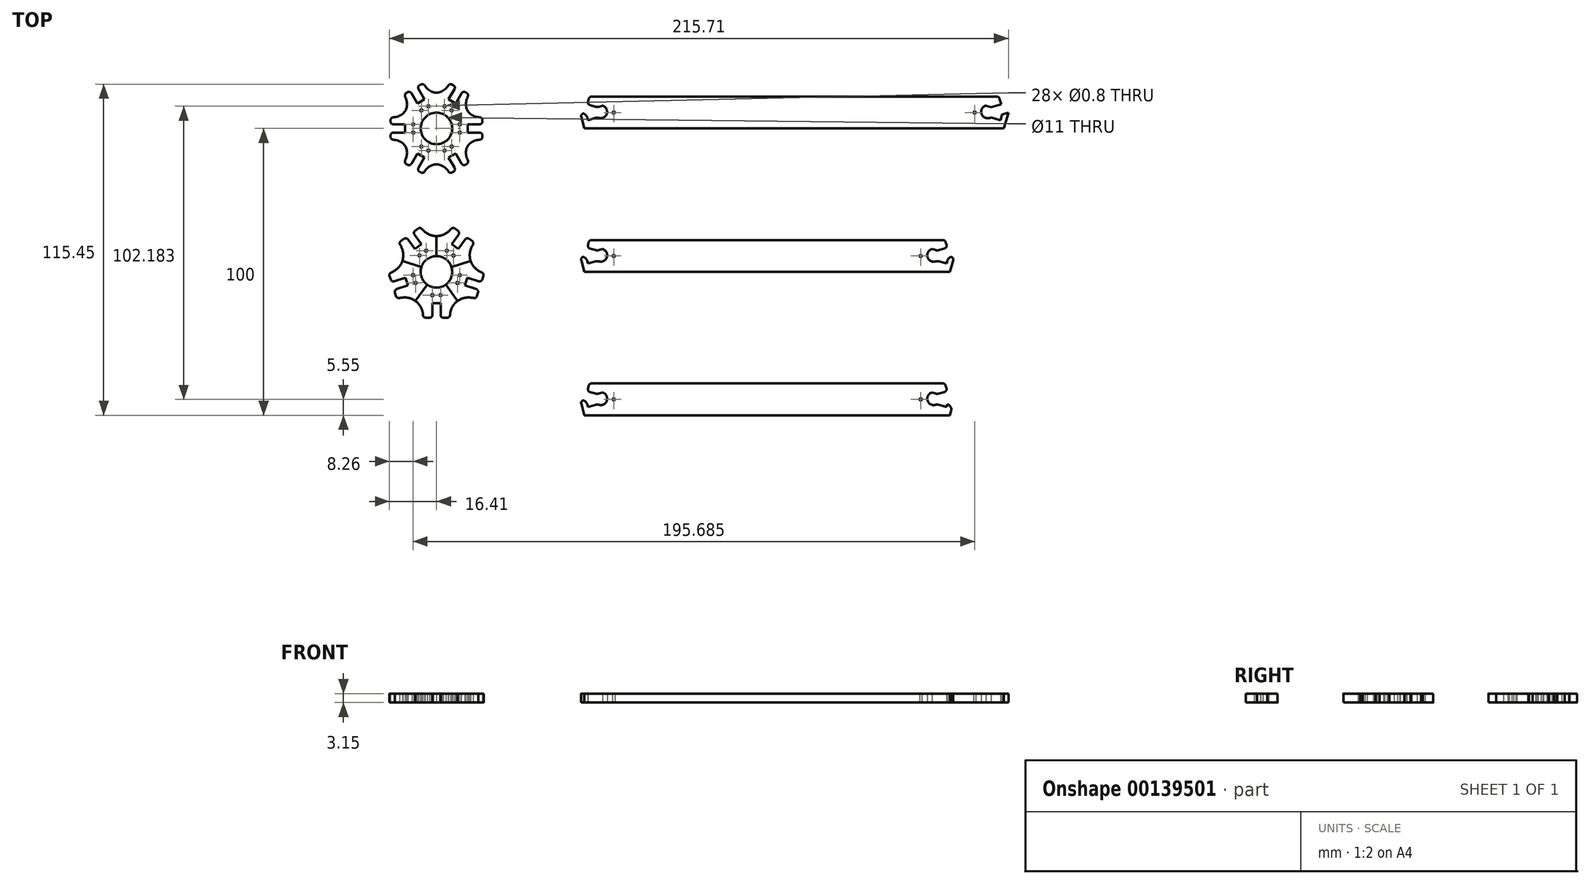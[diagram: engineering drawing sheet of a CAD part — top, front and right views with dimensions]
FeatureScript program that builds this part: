
annotation { "Feature Type Name" : "Feature", "Feature Type Description" : "" }
export const myFeature = defineFeature(function(context is Context, id is Id, definition is map)
    precondition{}
    {
        {
            assignVariable(context, id + "F0", {"name" : "wood_thickness", "anyValue" : 3.15 * mm});
        }
        {
            var Q0;
            Q0=qCreatedBy(makeId("Top.planeOp"),FACE);
            var sketch = newSketch(context, id + "F1", { "sketchPlane" : qUnion([Q0])});
            skArc(sketch, "E0", {"start": v(4.76, 2.75) * mm, "mid": v(2.75, 4.76) * mm, "end": v(0, 5.5) * mm});
            skArc(sketch, "E1", {"start": v(9.44, 5.45) * mm, "mid": v(5.45, 9.44) * mm, "end": v(0, 10.9) * mm, "construction": true});
            skLineSegment(sketch, "E2", {"start": v(0, 0) * mm, "end": v(0, 20) * mm, "construction": true});
            skLineSegment(sketch, "E3", {"start": v(0, 0) * mm, "end": v(17.32, 10) * mm, "construction": true});
            skPoint(sketch, "E4", {"position": v(0, 10.9) * mm});
            skPoint(sketch, "E5", {"position": v(0, 5.5) * mm});
            skPoint(sketch, "E6", {"position": v(9.44, 5.45) * mm});
            skPoint(sketch, "E7", {"position": v(4.76, 2.75) * mm});
            skLineSegment(sketch, "E8", {"start": v(5.48, 15.31) * mm, "end": v(5.9, 15.07) * mm});
            skLineSegment(sketch, "E9", {"start": v(6.27, 13.7) * mm, "end": v(4.22, 10.15) * mm});
            skLineSegment(sketch, "E10", {"start": v(6.68, 8.73) * mm, "end": v(8.73, 12.28) * mm});
            skLineSegment(sketch, "E11", {"start": v(10.1, 12.64) * mm, "end": v(10.52, 12.4) * mm});
            skPoint(sketch, "E12", {"position": v(0, 12.5) * mm});
            skEllipticalArc(sketch, "E13", {});
            skLineSegment(sketch, "E14", {"start": v(4.76, 2.75) * mm, "end": v(9.44, 5.45) * mm});
            skLineSegment(sketch, "E15", {"start": v(0, 5.5) * mm, "end": v(0, 10.9) * mm});
            skArc(sketch, "E16", {"start": v(10.83, 6.25) * mm, "mid": v(6.25, 10.83) * mm, "end": v(0, 12.5) * mm, "construction": true});
            skEllipticalArc(sketch, "E17", {});
            skLineSegment(sketch, "E18", {"start": v(0, 10.9) * mm, "end": v(0, 12.5) * mm});
            skLineSegment(sketch, "E19", {"start": v(9.44, 5.45) * mm, "end": v(10.83, 6.25) * mm});
            skPoint(sketch, "E20.visualSharp", {"position": v(4.62, 15.81) * mm});
            skArc(sketch, "E20.filletArc", {"start": v(5.48, 15.31) * mm, "mid": v(4.75, 15.42) * mm, "end": v(4.15, 15) * mm});
            skPoint(sketch, "E21.visualSharp", {"position": v(6.77, 14.57) * mm});
            skArc(sketch, "E21.filletArc", {"start": v(6.27, 13.7) * mm, "mid": v(6.37, 14.46) * mm, "end": v(5.9, 15.07) * mm});
            skLineSegment(sketch, "E22", {"start": v(4.15, 15) * mm, "end": v(6.3, 13.76) * mm, "construction": true});
            skLineSegment(sketch, "E23", {"start": v(4.15, 15) * mm, "end": v(4.62, 15.81) * mm, "construction": true});
            skLineSegment(sketch, "E24", {"start": v(4.62, 15.81) * mm, "end": v(5.48, 15.31) * mm, "construction": true});
            skArc(sketch, "E25.filletArc", {"start": v(10.92, 11.1) * mm, "mid": v(10.98, 11.82) * mm, "end": v(10.52, 12.4) * mm});
            skLineSegment(sketch, "E26", {"start": v(10.52, 12.4) * mm, "end": v(11.38, 11.9) * mm, "construction": true});
            skLineSegment(sketch, "E27", {"start": v(11.38, 11.9) * mm, "end": v(10.92, 11.1) * mm, "construction": true});
            skPoint(sketch, "E28.visualSharp", {"position": v(9.23, 13.14) * mm});
            skArc(sketch, "E28.filletArc", {"start": v(10.1, 12.64) * mm, "mid": v(9.34, 12.74) * mm, "end": v(8.73, 12.28) * mm});
            skLineSegment(sketch, "E29", {"start": v(4.22, 10.15) * mm, "end": v(5.45, 9.44) * mm});
            skLineSegment(sketch, "E30", {"start": v(5.45, 9.44) * mm, "end": v(6.68, 8.73) * mm});
            skLineSegment(sketch, "E31", {"start": v(10.92, 11.1) * mm, "end": v(8.77, 12.33) * mm, "construction": true});
            skLineSegment(sketch, "E32", {"start": v(4.22, 10.15) * mm, "end": v(1.42, 5.31) * mm, "construction": true});
            skLineSegment(sketch, "E33", {"start": v(3.9, 3.89) * mm, "end": v(6.68, 8.73) * mm, "construction": true});
            skCircle(sketch, "E34", {"center": v(2.82, 7.73) * mm, "radius": 0.4 * mm});
            skCircle(sketch, "E35", {"center": v(5.29, 6.3) * mm, "radius": 0.4 * mm});
            const initialGuessF1  = {"E13": [0, 0.02, 0, -1, 0.0075, 0.005564135286728559, 0, 0.8408323808141549], "E17": [0.017320508075688766, 0.01, -0.8660254037844385, -0.5, 0.0075, 0.005564135286728561, 5.44235292636543, 0]};
            skSetInitialGuess(sketch, initialGuessF1);
            skSolve(sketch);
        }
        {
            var Q0;
            Q0=makeQuery(id+"F1.imprint","IMPRINT",FACE,{"disambiguationData":[TD([[makeQuery(id+"F1.imprint","IMPRINT",EDGE,{"derivedFrom":sQuery(id+"F1.wireOp",EDGE,"E0")}),-1.0]])]});
            extrude(context, id + "F2", {"entities" : qUnion([Q0]), "depth" : getVariable(context, 'wood_thickness')});
        }
        {
            var Q0;
            Q0=qCreatedBy(makeId("Front.planeOp"),FACE);
            var sketch = newSketch(context, id + "F3", { "sketchPlane" : qUnion([Q0])});
            skLineSegment(sketch, "E36", {"start": v(0, 0) * mm, "end": v(0, 20) * mm});
            skSolve(sketch);
        }
        {
            var Q0;
            Q0=makeQuery(id+"F2.opExtrude","SWEPT_BODY",BODY,{"disambiguationData":[OSD([sQuery(id+"F1.wireOp",EDGE,"E0"),sQuery(id+"F1.wireOp",EDGE,"E8"),sQuery(id+"F1.wireOp",EDGE,"E9"),sQuery(id+"F1.wireOp",EDGE,"mfKBiNOg-JzFv-5jMB-imMp-SPBcFm9SmBFP"),sQuery(id+"F1.wireOp",EDGE,"E10"),sQuery(id+"F1.wireOp",EDGE,"E11"),sQuery(id+"F1.wireOp",EDGE,"E13"),sQuery(id+"F1.wireOp",EDGE,"E14"),sQuery(id+"F1.wireOp",EDGE,"E15"),sQuery(id+"F1.wireOp",EDGE,"E17"),sQuery(id+"F1.wireOp",EDGE,"E18"),sQuery(id+"F1.wireOp",EDGE,"E19")])]});
            var Q1;
            Q1=sQuery(id+"F3.wireOp",EDGE,"E36");
            circularPattern(context, id + "F4", {"operationType" : NewBodyOperationType.ADD, "entities" : qUnion([Q0]), "axis" : qUnion([Q1]), "angle" : 60 * degree, "instanceCount" : 6, "oppositeDirection" : true});
        }
        {
            var Q0;
            Q0=qCreatedBy(makeId("Top.planeOp"),FACE);
            var sketch = newSketch(context, id + "F5", { "sketchPlane" : qUnion([Q0])});
            skArc(sketch, "E37", {"start": v(5.23, -48.3) * mm, "mid": v(3.23, -45.55) * mm, "end": v(0, -44.5) * mm});
            skArc(sketch, "E38", {"start": v(10.37, -46.63) * mm, "mid": v(6.4, -41.18) * mm, "end": v(0, -39.1) * mm, "construction": true});
            skLineSegment(sketch, "E39", {"start": v(0, -50) * mm, "end": v(0, -30) * mm, "construction": true});
            skLineSegment(sketch, "E40", {"start": v(0, -50) * mm, "end": v(19.02, -43.82) * mm, "construction": true});
            skPoint(sketch, "E41", {"position": v(0, -39.1) * mm});
            skPoint(sketch, "E42", {"position": v(0, -44.5) * mm});
            skPoint(sketch, "E43", {"position": v(10.37, -46.63) * mm});
            skPoint(sketch, "E44", {"position": v(5.23, -48.3) * mm});
            skLineSegment(sketch, "E45", {"start": v(6.4, -34.88) * mm, "end": v(7.44, -35.63) * mm});
            skLineSegment(sketch, "E46", {"start": v(7.66, -37.03) * mm, "end": v(5.25, -40.34) * mm});
            skLineSegment(sketch, "E47", {"start": v(7.56, -42.02) * mm, "end": v(9.97, -38.7) * mm});
            skLineSegment(sketch, "E48", {"start": v(11.37, -38.48) * mm, "end": v(12.4, -39.23) * mm});
            skPoint(sketch, "E49", {"position": v(0, -37.5) * mm});
            skEllipticalArc(sketch, "E50", {});
            skLineSegment(sketch, "E51", {"start": v(5.23, -48.3) * mm, "end": v(10.37, -46.63) * mm});
            skLineSegment(sketch, "E52", {"start": v(0, -44.5) * mm, "end": v(0, -39.1) * mm});
            skArc(sketch, "E53", {"start": v(11.89, -46.14) * mm, "mid": v(7.35, -39.89) * mm, "end": v(0, -37.5) * mm, "construction": true});
            skEllipticalArc(sketch, "E54", {});
            skLineSegment(sketch, "E55", {"start": v(0, -39.1) * mm, "end": v(0, -37.5) * mm});
            skLineSegment(sketch, "E56", {"start": v(10.37, -46.63) * mm, "end": v(11.89, -46.14) * mm});
            skPoint(sketch, "E57.visualSharp", {"position": v(5.6, -34.3) * mm});
            skArc(sketch, "E57.filletArc", {"start": v(6.4, -34.88) * mm, "mid": v(5.7, -34.7) * mm, "end": v(5.05, -35.05) * mm});
            skPoint(sketch, "E58.visualSharp", {"position": v(8.25, -36.22) * mm});
            skArc(sketch, "E58.filletArc", {"start": v(7.66, -37.03) * mm, "mid": v(7.84, -36.28) * mm, "end": v(7.44, -35.63) * mm});
            skLineSegment(sketch, "E59", {"start": v(5.05, -35.05) * mm, "end": v(7.7, -36.98) * mm, "construction": true});
            skLineSegment(sketch, "E60", {"start": v(5.05, -35.05) * mm, "end": v(5.6, -34.3) * mm, "construction": true});
            skLineSegment(sketch, "E61", {"start": v(5.6, -34.3) * mm, "end": v(6.4, -34.88) * mm, "construction": true});
            skArc(sketch, "E62.filletArc", {"start": v(12.66, -40.58) * mm, "mid": v(12.8, -39.86) * mm, "end": v(12.4, -39.23) * mm});
            skLineSegment(sketch, "E63", {"start": v(12.4, -39.23) * mm, "end": v(13.21, -39.82) * mm, "construction": true});
            skLineSegment(sketch, "E64", {"start": v(13.21, -39.82) * mm, "end": v(12.66, -40.58) * mm, "construction": true});
            skPoint(sketch, "E65.visualSharp", {"position": v(10.56, -37.9) * mm});
            skArc(sketch, "E65.filletArc", {"start": v(11.37, -38.48) * mm, "mid": v(10.62, -38.3) * mm, "end": v(9.97, -38.7) * mm});
            skLineSegment(sketch, "E66", {"start": v(5.25, -40.34) * mm, "end": v(6.4, -41.18) * mm});
            skLineSegment(sketch, "E67", {"start": v(6.4, -41.18) * mm, "end": v(7.56, -42.02) * mm});
            skLineSegment(sketch, "E68", {"start": v(12.66, -40.58) * mm, "end": v(10, -38.65) * mm, "construction": true});
            skLineSegment(sketch, "E69", {"start": v(5.25, -40.34) * mm, "end": v(1.97, -44.86) * mm, "construction": true});
            skLineSegment(sketch, "E70", {"start": v(4.28, -46.54) * mm, "end": v(7.56, -42.02) * mm, "construction": true});
            skCircle(sketch, "E71", {"center": v(3.61, -42.6) * mm, "radius": 0.4 * mm});
            skCircle(sketch, "E72", {"center": v(5.92, -44.28) * mm, "radius": 0.4 * mm});
            const initialGuessF5  = {"E50": [0, -0.03, 0, -1, 0.0075, 0.006825802079921419, 0, 0.832408500908553], "E54": [0.019021130325903073, -0.043819660112501053, -0.9510565162951536, -0.3090169943749476, 0.0075, 0.006825802079921406, 5.450776806271033, 0]};
            skSetInitialGuess(sketch, initialGuessF5);
            skSolve(sketch);
        }
        {
            var Q0;
            Q0=makeQuery(id+"F5.imprint","IMPRINT",FACE,{"disambiguationData":[TD([[makeQuery(id+"F5.imprint","IMPRINT",EDGE,{"derivedFrom":sQuery(id+"F5.wireOp",EDGE,"E37")}),-1.0]])]});
            extrude(context, id + "F6", {"entities" : qUnion([Q0]), "depth" : getVariable(context, 'wood_thickness')});
        }
        {
            var Q0;
            Q0=qCreatedBy(makeId("Front.planeOp"),FACE);
            var Q1;
            Q1=sQuery(id+"F5.wireOp",VERTEX,"E40.start");
            cPlane(context, id + "F7", {"entities" : qUnion([Q0, Q1]), "cplaneType" : CPlaneType.PLANE_POINT, "offset" : 25 * mm, "width" : 150 * mm, "height" : 150 * mm});
        }
        {
            var Q0;
            Q0=qCreatedBy(id+"F7.planeOp",FACE);
            var sketch = newSketch(context, id + "F8", { "sketchPlane" : qUnion([Q0])});
            skLineSegment(sketch, "E73", {"start": v(0, 0) * mm, "end": v(0, 50) * mm});
            skSolve(sketch);
        }
        {
            var Q0;
            Q0=makeQuery(id+"F6.opExtrude","SWEPT_BODY",BODY,{"disambiguationData":[OSD([sQuery(id+"F5.wireOp",EDGE,"E37"),sQuery(id+"F5.wireOp",EDGE,"E45"),sQuery(id+"F5.wireOp",EDGE,"E46"),sQuery(id+"F5.wireOp",EDGE,"E47"),sQuery(id+"F5.wireOp",EDGE,"E48"),sQuery(id+"F5.wireOp",EDGE,"E50"),sQuery(id+"F5.wireOp",EDGE,"E51"),sQuery(id+"F5.wireOp",EDGE,"E52"),sQuery(id+"F5.wireOp",EDGE,"E54"),sQuery(id+"F5.wireOp",EDGE,"E55"),sQuery(id+"F5.wireOp",EDGE,"E56"),sQuery(id+"F5.wireOp",EDGE,"E57.filletArc"),sQuery(id+"F5.wireOp",EDGE,"E58.filletArc"),sQuery(id+"F5.wireOp",EDGE,"E62.filletArc"),sQuery(id+"F5.wireOp",EDGE,"E65.filletArc"),sQuery(id+"F5.wireOp",EDGE,"E66"),sQuery(id+"F5.wireOp",EDGE,"E67"),sQuery(id+"F5.wireOp",EDGE,"E71"),sQuery(id+"F5.wireOp",EDGE,"E72")])]});
            var Q1;
            Q1=sQuery(id+"F8.wireOp",EDGE,"E73");
            circularPattern(context, id + "F9", {"operationType" : NewBodyOperationType.ADD, "entities" : qUnion([Q0]), "axis" : qUnion([Q1]), "angle" : 72 * degree, "instanceCount" : 5});
        }
        {
            var Q0;
            Q0=qCreatedBy(makeId("Top.planeOp"),FACE);
            var sketch = newSketch(context, id + "F10", { "sketchPlane" : qUnion([Q0])});
            skLineSegment(sketch, "E74", {"start": v(0, 0) * mm, "end": v(50, 0) * mm, "construction": true});
            skLineSegment(sketch, "E75", {"start": v(50, 0) * mm, "end": v(50, 11.1) * mm, "construction": true});
            skLineSegment(sketch, "E76", {"start": v(50, 0) * mm, "end": v(124.65, 0) * mm, "construction": true});
            skLineSegment(sketch, "E77", {"start": v(50, 11.1) * mm, "end": v(124.65, 11.1) * mm, "construction": true});
            skLineSegment(sketch, "E78", {"start": v(124.65, 11.1) * mm, "end": v(124.65, 0) * mm, "construction": true});
            skLineSegment(sketch, "E79", {"start": v(51.6, 0) * mm, "end": v(50, 5.55) * mm});
            skLineSegment(sketch, "E80", {"start": v(50, 5.55) * mm, "end": v(52.19, 4.92) * mm});
            skLineSegment(sketch, "E81", {"start": v(52.19, 4.92) * mm, "end": v(52.77, 2.9) * mm});
            skLineSegment(sketch, "E82", {"start": v(52.77, 2.9) * mm, "end": v(56, 3.83) * mm});
            skLineSegment(sketch, "E83", {"start": v(56, 3.83) * mm, "end": v(56.6, 3.66) * mm});
            skLineSegment(sketch, "E84", {"start": v(56.6, 3.66) * mm, "end": v(58.92, 4.32) * mm, "construction": true});
            skLineSegment(sketch, "E85", {"start": v(58.92, 4.32) * mm, "end": v(57.87, 7.95) * mm, "construction": true});
            skLineSegment(sketch, "E86", {"start": v(57.87, 7.95) * mm, "end": v(56, 7.42) * mm});
            skLineSegment(sketch, "E87", {"start": v(56, 7.42) * mm, "end": v(52.5, 8.42) * mm});
            skLineSegment(sketch, "E88", {"start": v(52.5, 8.42) * mm, "end": v(53.27, 11.1) * mm});
            skLineSegment(sketch, "E89", {"start": v(51.6, 0) * mm, "end": v(197.7, 0) * mm});
            skLineSegment(sketch, "E90", {"start": v(53.27, 11.1) * mm, "end": v(196.03, 11.1) * mm});
            skLineSegment(sketch, "E91", {"start": v(56.6, 3.66) * mm, "end": v(57.87, 7.95) * mm, "construction": true});
            skArc(sketch, "E92", {"start": v(57.87, 7.95) * mm, "mid": v(59.39, 5.17) * mm, "end": v(56.6, 3.66) * mm});
            skPoint(sketch, "E93.endSnap0", {"position": v(51.1, 5.24) * mm});
            skLineSegment(sketch, "E94.MirrorCS", {"start": v(197.7, 0) * mm, "end": v(199.3, 5.55) * mm});
            skLineSegment(sketch, "E95.MirrorCS", {"start": v(199.3, 5.55) * mm, "end": v(197.11, 4.92) * mm});
            skLineSegment(sketch, "E96.MirrorCS", {"start": v(197.11, 4.92) * mm, "end": v(196.53, 2.9) * mm});
            skLineSegment(sketch, "E97.MirrorCS", {"start": v(196.53, 2.9) * mm, "end": v(193.3, 3.83) * mm});
            skLineSegment(sketch, "E98.MirrorCS", {"start": v(193.3, 3.83) * mm, "end": v(192.7, 3.66) * mm});
            skArc(sketch, "E99.MirrorCS", {"start": v(191.43, 7.95) * mm, "mid": v(189.91, 5.17) * mm, "end": v(192.7, 3.66) * mm});
            skLineSegment(sketch, "E100.MirrorCS", {"start": v(191.43, 7.95) * mm, "end": v(193.3, 7.42) * mm});
            skLineSegment(sketch, "E101.MirrorCS", {"start": v(193.3, 7.42) * mm, "end": v(196.8, 8.42) * mm});
            skLineSegment(sketch, "E102.MirrorCS", {"start": v(196.8, 8.42) * mm, "end": v(196.03, 11.1) * mm});
            skLineSegment(sketch, "E103", {"start": v(50, 5.55) * mm, "end": v(199.3, 5.55) * mm, "construction": true});
            skCircle(sketch, "E104", {"center": v(187.54, 5.55) * mm, "radius": 0.4 * mm});
            skCircle(sketch, "E105", {"center": v(61.76, 5.55) * mm, "radius": 0.4 * mm});
            skLineSegment(sketch, "E106", {"start": v(61.76, 5.55) * mm, "end": v(59.46, 5.55) * mm, "construction": true});
            skLineSegment(sketch, "E107", {"start": v(187.54, 5.55) * mm, "end": v(189.84, 5.55) * mm, "construction": true});
            skSolve(sketch);
        }
        {
            var Q0;
            Q0=makeQuery(id+"F10.imprint","IMPRINT",FACE,{"disambiguationData":[TD([[makeQuery(id+"F10.imprint","IMPRINT",EDGE,{"derivedFrom":sQuery(id+"F10.wireOp",EDGE,"E79")}),-1.0]])]});
            extrude(context, id + "F11", {"entities" : qUnion([Q0]), "depth" : getVariable(context, 'wood_thickness')});
        }
        {
            var Q0;
            Q0=makeQuery(id+"F11.opExtrude","SWEPT_EDGE",EDGE,{"disambiguationData":[OSD([sQuery(id+"F10.wireOp",EDGE,"E86"),sQuery(id+"F10.wireOp",EDGE,"E87")])]});
            var Q1;
            Q1=makeQuery(id+"F11.opExtrude","SWEPT_EDGE",EDGE,{"disambiguationData":[OSD([sQuery(id+"F10.wireOp",EDGE,"E82"),sQuery(id+"F10.wireOp",EDGE,"E83")])]});
            var Q2;
            Q2=makeQuery(id+"F11.opExtrude","SWEPT_EDGE",EDGE,{"disambiguationData":[OSD([sQuery(id+"F10.wireOp",EDGE,"E80"),sQuery(id+"F10.wireOp",EDGE,"E81")])]});
            var Q3;
            Q3=makeQuery(id+"F11.opExtrude","SWEPT_EDGE",EDGE,{"disambiguationData":[OSD([sQuery(id+"F10.wireOp",EDGE,"ecbd6355-1247-42db-afb2-b917e20613ce0.MirrorCS"),sQuery(id+"F10.wireOp",EDGE,"ef6c834d-02ef-4d6f-9716-54fc313d26910.MirrorCS")])]});
            var Q4;
            Q4=makeQuery(id+"F11.opExtrude","SWEPT_EDGE",EDGE,{"disambiguationData":[OSD([sQuery(id+"F10.wireOp",EDGE,"c2f2e863-0dd1-41ea-9a90-eeab5b9333880.MirrorCS"),sQuery(id+"F10.wireOp",EDGE,"853300a5-473e-431b-ac92-eafcaa067bd40.MirrorCS")])]});
            var Q5;
            Q5=makeQuery(id+"F11.opExtrude","SWEPT_EDGE",EDGE,{"disambiguationData":[OSD([sQuery(id+"F10.wireOp",EDGE,"4ca5c7fb-cf56-4dfb-8872-57cf61e489230.MirrorCS"),sQuery(id+"F10.wireOp",EDGE,"298d15c9-40d8-42b4-a12f-17c602055c9c0.MirrorCS")])]});
            fillet(context, id + "F12", {"entities" : qUnion([Q0, Q1, Q2, Q3, Q4, Q5]), "radius" : 2 * mm, "tangentPropagation" : true, "allowEdgeOverflow" : false});
        }
        {
            var Q0;
            Q0=makeQuery(id+"F11.opExtrude","SWEPT_EDGE",EDGE,{"disambiguationData":[OSD([sQuery(id+"F10.wireOp",EDGE,"E79"),sQuery(id+"F10.wireOp",EDGE,"E80")])]});
            var Q1;
            Q1=makeQuery(id+"F11.opExtrude","SWEPT_EDGE",EDGE,{"disambiguationData":[OSD([sQuery(id+"F10.wireOp",EDGE,"E87"),sQuery(id+"F10.wireOp",EDGE,"E88")])]});
            var Q2;
            Q2=makeQuery(id+"F11.opExtrude","SWEPT_EDGE",EDGE,{"disambiguationData":[OSD([sQuery(id+"F10.wireOp",EDGE,"E88"),sQuery(id+"F10.wireOp",EDGE,"E90")])]});
            var Q3;
            Q3=makeQuery(id+"F11.opExtrude","SWEPT_EDGE",EDGE,{"disambiguationData":[OSD([sQuery(id+"F10.wireOp",EDGE,"58fe3ff1-e28c-4c06-9c65-c541867c6f450.MirrorCS"),sQuery(id+"F10.wireOp",EDGE,"4ca5c7fb-cf56-4dfb-8872-57cf61e489230.MirrorCS")])]});
            var Q4;
            Q4=makeQuery(id+"F11.opExtrude","SWEPT_EDGE",EDGE,{"disambiguationData":[OSD([sQuery(id+"F10.wireOp",EDGE,"853300a5-473e-431b-ac92-eafcaa067bd40.MirrorCS"),sQuery(id+"F10.wireOp",EDGE,"cfe77f50-aeba-4152-badc-bec2262164020.MirrorCS")])]});
            var Q5;
            Q5=makeQuery(id+"F11.opExtrude","SWEPT_EDGE",EDGE,{"disambiguationData":[OSD([sQuery(id+"F10.wireOp",EDGE,"cfe77f50-aeba-4152-badc-bec2262164020.MirrorCS"),sQuery(id+"F10.wireOp",EDGE,"E90")])]});
            fillet(context, id + "F13", {"entities" : qUnion([Q0, Q1, Q2, Q3, Q4, Q5]), "radius" : 1 * mm, "tangentPropagation" : true, "allowEdgeOverflow" : false});
        }
        {
            var Q0;
            Q0=qCreatedBy(makeId("Top.planeOp"),FACE);
            var sketch = newSketch(context, id + "F14", { "sketchPlane" : qUnion([Q0])});
            skLineSegment(sketch, "E108", {"start": v(0, -50) * mm, "end": v(50, -50) * mm, "construction": true});
            skLineSegment(sketch, "E109", {"start": v(50, -50) * mm, "end": v(50, -38.9) * mm, "construction": true});
            skLineSegment(sketch, "E110", {"start": v(50, -50) * mm, "end": v(115.25, -50) * mm, "construction": true});
            skLineSegment(sketch, "E111", {"start": v(50, -38.9) * mm, "end": v(115.25, -38.9) * mm, "construction": true});
            skLineSegment(sketch, "E112", {"start": v(115.25, -38.9) * mm, "end": v(115.25, -50) * mm, "construction": true});
            skLineSegment(sketch, "E113", {"start": v(51.6, -50) * mm, "end": v(50, -44.45) * mm});
            skLineSegment(sketch, "E114", {"start": v(50, -44.45) * mm, "end": v(52.19, -45.08) * mm});
            skLineSegment(sketch, "E115", {"start": v(52.19, -45.08) * mm, "end": v(52.77, -47.1) * mm});
            skLineSegment(sketch, "E116", {"start": v(52.77, -47.1) * mm, "end": v(56, -46.17) * mm});
            skLineSegment(sketch, "E117", {"start": v(56, -46.17) * mm, "end": v(56.6, -46.34) * mm});
            skLineSegment(sketch, "E118", {"start": v(56.6, -46.34) * mm, "end": v(58.92, -45.68) * mm, "construction": true});
            skLineSegment(sketch, "E119", {"start": v(58.92, -45.68) * mm, "end": v(57.87, -42.05) * mm, "construction": true});
            skLineSegment(sketch, "E120", {"start": v(57.87, -42.05) * mm, "end": v(56, -42.58) * mm});
            skLineSegment(sketch, "E121", {"start": v(56, -42.58) * mm, "end": v(52.5, -41.58) * mm});
            skLineSegment(sketch, "E122", {"start": v(52.5, -41.58) * mm, "end": v(53.27, -38.9) * mm});
            skLineSegment(sketch, "E123", {"start": v(51.6, -50) * mm, "end": v(178.9, -50) * mm});
            skLineSegment(sketch, "E124", {"start": v(53.27, -38.9) * mm, "end": v(177.23, -38.9) * mm});
            skLineSegment(sketch, "E125", {"start": v(56.6, -46.34) * mm, "end": v(57.87, -42.05) * mm, "construction": true});
            skArc(sketch, "E126", {"start": v(57.87, -42.05) * mm, "mid": v(59.39, -44.83) * mm, "end": v(56.6, -46.34) * mm});
            skPoint(sketch, "E127.endSnap0", {"position": v(51.1, -44.76) * mm});
            skLineSegment(sketch, "E128.MirrorCS", {"start": v(178.9, -50) * mm, "end": v(180.5, -44.45) * mm});
            skLineSegment(sketch, "E129.MirrorCS", {"start": v(180.5, -44.45) * mm, "end": v(178.31, -45.08) * mm});
            skLineSegment(sketch, "E130.MirrorCS", {"start": v(178.31, -45.08) * mm, "end": v(177.73, -47.1) * mm});
            skLineSegment(sketch, "E131.MirrorCS", {"start": v(177.73, -47.1) * mm, "end": v(174.5, -46.17) * mm});
            skLineSegment(sketch, "E132.MirrorCS", {"start": v(174.5, -46.17) * mm, "end": v(173.9, -46.34) * mm});
            skArc(sketch, "E133.MirrorCS", {"start": v(172.63, -42.05) * mm, "mid": v(171.11, -44.83) * mm, "end": v(173.9, -46.34) * mm});
            skLineSegment(sketch, "E134.MirrorCS", {"start": v(172.63, -42.05) * mm, "end": v(174.5, -42.58) * mm});
            skLineSegment(sketch, "E135.MirrorCS", {"start": v(174.5, -42.58) * mm, "end": v(178, -41.58) * mm});
            skLineSegment(sketch, "E136.MirrorCS", {"start": v(178, -41.58) * mm, "end": v(177.23, -38.9) * mm});
            skLineSegment(sketch, "E137", {"start": v(50, -44.45) * mm, "end": v(180.5, -44.45) * mm, "construction": true});
            skCircle(sketch, "E138", {"center": v(168.74, -44.45) * mm, "radius": 0.4 * mm});
            skCircle(sketch, "E139", {"center": v(61.76, -44.45) * mm, "radius": 0.4 * mm});
            skLineSegment(sketch, "E140", {"start": v(61.76, -44.45) * mm, "end": v(59.46, -44.45) * mm, "construction": true});
            skLineSegment(sketch, "E141", {"start": v(168.74, -44.45) * mm, "end": v(171.04, -44.45) * mm, "construction": true});
            skLineSegment(sketch, "E142", {"start": v(0, -50) * mm, "end": v(0, 0) * mm, "construction": true});
            skSolve(sketch);
        }
        {
            var Q0;
            Q0=makeQuery(id+"F14.imprint","IMPRINT",FACE,{"disambiguationData":[TD([[makeQuery(id+"F14.imprint","IMPRINT",EDGE,{"derivedFrom":sQuery(id+"F14.wireOp",EDGE,"E113")}),-1.0]])]});
            extrude(context, id + "F15", {"entities" : qUnion([Q0]), "depth" : getVariable(context, 'wood_thickness')});
        }
        {
            var Q0;
            Q0=makeQuery(id+"F15.opExtrude","SWEPT_EDGE",EDGE,{"disambiguationData":[OSD([sQuery(id+"F14.wireOp",EDGE,"E114"),sQuery(id+"F14.wireOp",EDGE,"E115")])]});
            var Q1;
            Q1=makeQuery(id+"F15.opExtrude","SWEPT_EDGE",EDGE,{"disambiguationData":[OSD([sQuery(id+"F14.wireOp",EDGE,"E116"),sQuery(id+"F14.wireOp",EDGE,"E117")])]});
            var Q2;
            Q2=makeQuery(id+"F15.opExtrude","SWEPT_EDGE",EDGE,{"disambiguationData":[OSD([sQuery(id+"F14.wireOp",EDGE,"E120"),sQuery(id+"F14.wireOp",EDGE,"E121")])]});
            var Q3;
            Q3=makeQuery(id+"F15.opExtrude","SWEPT_EDGE",EDGE,{"disambiguationData":[OSD([sQuery(id+"F14.wireOp",EDGE,"E134.MirrorCS"),sQuery(id+"F14.wireOp",EDGE,"E135.MirrorCS")])]});
            var Q4;
            Q4=makeQuery(id+"F15.opExtrude","SWEPT_EDGE",EDGE,{"disambiguationData":[OSD([sQuery(id+"F14.wireOp",EDGE,"E131.MirrorCS"),sQuery(id+"F14.wireOp",EDGE,"E132.MirrorCS")])]});
            var Q5;
            Q5=makeQuery(id+"F15.opExtrude","SWEPT_EDGE",EDGE,{"disambiguationData":[OSD([sQuery(id+"F14.wireOp",EDGE,"E129.MirrorCS"),sQuery(id+"F14.wireOp",EDGE,"E130.MirrorCS")])]});
            fillet(context, id + "F16", {"entities" : qUnion([Q0, Q1, Q2, Q3, Q4, Q5]), "radius" : 2 * mm, "tangentPropagation" : true, "allowEdgeOverflow" : false});
        }
        {
            var Q0;
            Q0=makeQuery(id+"F15.opExtrude","SWEPT_EDGE",EDGE,{"disambiguationData":[OSD([sQuery(id+"F14.wireOp",EDGE,"E124"),sQuery(id+"F14.wireOp",EDGE,"E136.MirrorCS")])]});
            var Q1;
            Q1=makeQuery(id+"F15.opExtrude","SWEPT_EDGE",EDGE,{"disambiguationData":[OSD([sQuery(id+"F14.wireOp",EDGE,"E135.MirrorCS"),sQuery(id+"F14.wireOp",EDGE,"E136.MirrorCS")])]});
            var Q2;
            Q2=makeQuery(id+"F15.opExtrude","SWEPT_EDGE",EDGE,{"disambiguationData":[OSD([sQuery(id+"F14.wireOp",EDGE,"E128.MirrorCS"),sQuery(id+"F14.wireOp",EDGE,"E129.MirrorCS")])]});
            var Q3;
            Q3=makeQuery(id+"F15.opExtrude","SWEPT_EDGE",EDGE,{"disambiguationData":[OSD([sQuery(id+"F14.wireOp",EDGE,"E122"),sQuery(id+"F14.wireOp",EDGE,"E124")])]});
            var Q4;
            Q4=makeQuery(id+"F15.opExtrude","SWEPT_EDGE",EDGE,{"disambiguationData":[OSD([sQuery(id+"F14.wireOp",EDGE,"E113"),sQuery(id+"F14.wireOp",EDGE,"E114")])]});
            var Q5;
            Q5=makeQuery(id+"F15.opExtrude","SWEPT_EDGE",EDGE,{"disambiguationData":[OSD([sQuery(id+"F14.wireOp",EDGE,"E121"),sQuery(id+"F14.wireOp",EDGE,"E122")])]});
            fillet(context, id + "F17", {"entities" : qUnion([Q0, Q1, Q2, Q3, Q4, Q5]), "radius" : 1 * mm, "tangentPropagation" : true, "allowEdgeOverflow" : false});
        }
        {
            var Q0;
            Q0=qCreatedBy(makeId("Top.planeOp"),FACE);
            var sketch = newSketch(context, id + "F18", { "sketchPlane" : qUnion([Q0])});
            skLineSegment(sketch, "E143", {"start": v(0, -100) * mm, "end": v(50, -100) * mm, "construction": true});
            skLineSegment(sketch, "E144", {"start": v(50, -100) * mm, "end": v(50, -88.9) * mm, "construction": true});
            skLineSegment(sketch, "E145", {"start": v(50, -100) * mm, "end": v(115.25, -100) * mm, "construction": true});
            skLineSegment(sketch, "E146", {"start": v(50, -88.9) * mm, "end": v(115.25, -88.9) * mm, "construction": true});
            skLineSegment(sketch, "E147", {"start": v(115.25, -88.9) * mm, "end": v(115.25, -100) * mm, "construction": true});
            skLineSegment(sketch, "E148", {"start": v(51.6, -100) * mm, "end": v(50, -94.45) * mm});
            skLineSegment(sketch, "E149", {"start": v(50, -94.45) * mm, "end": v(52.19, -95.08) * mm});
            skLineSegment(sketch, "E150", {"start": v(52.19, -95.08) * mm, "end": v(52.77, -97.1) * mm});
            skLineSegment(sketch, "E151", {"start": v(52.77, -97.1) * mm, "end": v(56, -96.17) * mm});
            skLineSegment(sketch, "E152", {"start": v(56, -96.17) * mm, "end": v(56.6, -96.34) * mm});
            skLineSegment(sketch, "E153", {"start": v(56.6, -96.34) * mm, "end": v(58.92, -95.68) * mm, "construction": true});
            skLineSegment(sketch, "E154", {"start": v(58.92, -95.68) * mm, "end": v(57.87, -92.05) * mm, "construction": true});
            skLineSegment(sketch, "E155", {"start": v(57.87, -92.05) * mm, "end": v(56, -92.58) * mm});
            skLineSegment(sketch, "E156", {"start": v(56, -92.58) * mm, "end": v(52.5, -91.58) * mm});
            skLineSegment(sketch, "E157", {"start": v(52.5, -91.58) * mm, "end": v(53.27, -88.9) * mm});
            skLineSegment(sketch, "E158", {"start": v(51.6, -100) * mm, "end": v(178.9, -100) * mm});
            skLineSegment(sketch, "E159", {"start": v(53.27, -88.9) * mm, "end": v(177.23, -88.9) * mm});
            skLineSegment(sketch, "E160", {"start": v(56.6, -96.34) * mm, "end": v(57.87, -92.05) * mm, "construction": true});
            skArc(sketch, "E161", {"start": v(57.87, -92.05) * mm, "mid": v(59.39, -94.83) * mm, "end": v(56.6, -96.34) * mm});
            skPoint(sketch, "E162.endSnap0", {"position": v(51.1, -94.76) * mm});
            skLineSegment(sketch, "E163.MirrorCS", {"start": v(178.9, -100) * mm, "end": v(180.5, -94.45) * mm, "construction": true});
            skLineSegment(sketch, "E164.MirrorCS", {"start": v(180.5, -94.45) * mm, "end": v(178.31, -95.08) * mm, "construction": true});
            skLineSegment(sketch, "E165.MirrorCS", {"start": v(178.31, -95.08) * mm, "end": v(177.73, -97.1) * mm, "construction": true});
            skLineSegment(sketch, "E166.MirrorCS", {"start": v(177.73, -97.1) * mm, "end": v(174.5, -96.17) * mm});
            skLineSegment(sketch, "E167.MirrorCS", {"start": v(174.5, -96.17) * mm, "end": v(173.9, -96.34) * mm});
            skArc(sketch, "E168.MirrorCS", {"start": v(172.63, -92.05) * mm, "mid": v(171.11, -94.83) * mm, "end": v(173.9, -96.34) * mm});
            skLineSegment(sketch, "E169.MirrorCS", {"start": v(172.63, -92.05) * mm, "end": v(174.5, -92.58) * mm});
            skLineSegment(sketch, "E170.MirrorCS", {"start": v(174.5, -92.58) * mm, "end": v(178, -91.58) * mm});
            skLineSegment(sketch, "E171.MirrorCS", {"start": v(178, -91.58) * mm, "end": v(177.23, -88.9) * mm});
            skLineSegment(sketch, "E172", {"start": v(50, -94.45) * mm, "end": v(180.5, -94.45) * mm, "construction": true});
            skCircle(sketch, "E173", {"center": v(168.74, -94.45) * mm, "radius": 0.4 * mm});
            skCircle(sketch, "E174", {"center": v(61.76, -94.45) * mm, "radius": 0.4 * mm});
            skLineSegment(sketch, "E175", {"start": v(61.76, -94.45) * mm, "end": v(59.46, -94.45) * mm, "construction": true});
            skLineSegment(sketch, "E176", {"start": v(168.74, -94.45) * mm, "end": v(171.04, -94.45) * mm, "construction": true});
            skLineSegment(sketch, "E177", {"start": v(0, -100) * mm, "end": v(0, 0) * mm, "construction": true});
            skLineSegment(sketch, "E178", {"start": v(178.31, -95.08) * mm, "end": v(180.17, -95.6) * mm, "construction": true});
            skLineSegment(sketch, "E179", {"start": v(178.02, -96.09) * mm, "end": v(179.88, -96.62) * mm});
            skLineSegment(sketch, "E180", {"start": v(177.73, -97.1) * mm, "end": v(178.02, -96.09) * mm});
            skLineSegment(sketch, "E181", {"start": v(179.88, -96.62) * mm, "end": v(178.9, -100) * mm});
            skSolve(sketch);
        }
        {
            var Q0;
            Q0=makeQuery(id+"F18.imprint","IMPRINT",FACE,{"disambiguationData":[TD([[makeQuery(id+"F18.imprint","IMPRINT",EDGE,{"derivedFrom":sQuery(id+"F18.wireOp",EDGE,"E148")}),-1.0]])]});
            extrude(context, id + "F19", {"entities" : qUnion([Q0]), "depth" : getVariable(context, 'wood_thickness')});
        }
        {
            var Q0;
            Q0=makeQuery(id+"F19.opExtrude","SWEPT_EDGE",EDGE,{"disambiguationData":[OSD([sQuery(id+"F18.wireOp",EDGE,"E166.MirrorCS"),sQuery(id+"F18.wireOp",EDGE,"E167.MirrorCS")])]});
            var Q1;
            Q1=makeQuery(id+"F19.opExtrude","SWEPT_EDGE",EDGE,{"disambiguationData":[OSD([sQuery(id+"F18.wireOp",EDGE,"E169.MirrorCS"),sQuery(id+"F18.wireOp",EDGE,"E170.MirrorCS")])]});
            var Q2;
            Q2=makeQuery(id+"F19.opExtrude","SWEPT_EDGE",EDGE,{"disambiguationData":[OSD([sQuery(id+"F18.wireOp",EDGE,"E155"),sQuery(id+"F18.wireOp",EDGE,"E156")])]});
            var Q3;
            Q3=makeQuery(id+"F19.opExtrude","SWEPT_EDGE",EDGE,{"disambiguationData":[OSD([sQuery(id+"F18.wireOp",EDGE,"E151"),sQuery(id+"F18.wireOp",EDGE,"E152")])]});
            var Q4;
            Q4=makeQuery(id+"F19.opExtrude","SWEPT_EDGE",EDGE,{"disambiguationData":[OSD([sQuery(id+"F18.wireOp",EDGE,"E149"),sQuery(id+"F18.wireOp",EDGE,"E150")])]});
            var Q5;
            Q5=makeQuery(id+"F19.opExtrude","SWEPT_EDGE",EDGE,{"disambiguationData":[OSD([sQuery(id+"F18.wireOp",EDGE,"E179"),sQuery(id+"F18.wireOp",EDGE,"E181")])]});
            fillet(context, id + "F20", {"entities" : qUnion([Q0, Q1, Q2, Q3, Q4, Q5]), "radius" : 2 * mm, "tangentPropagation" : true, "allowEdgeOverflow" : false});
        }
        {
            var Q0;
            Q0=makeQuery(id+"F19.opExtrude","SWEPT_EDGE",EDGE,{"disambiguationData":[OSD([sQuery(id+"F18.wireOp",EDGE,"E159"),sQuery(id+"F18.wireOp",EDGE,"E171.MirrorCS")])]});
            var Q1;
            Q1=makeQuery(id+"F19.opExtrude","SWEPT_EDGE",EDGE,{"disambiguationData":[OSD([sQuery(id+"F18.wireOp",EDGE,"E170.MirrorCS"),sQuery(id+"F18.wireOp",EDGE,"E171.MirrorCS")])]});
            var Q2;
            Q2=makeQuery(id+"F19.opExtrude","SWEPT_EDGE",EDGE,{"disambiguationData":[OSD([sQuery(id+"F18.wireOp",EDGE,"E157"),sQuery(id+"F18.wireOp",EDGE,"E159")])]});
            var Q3;
            Q3=makeQuery(id+"F19.opExtrude","SWEPT_EDGE",EDGE,{"disambiguationData":[OSD([sQuery(id+"F18.wireOp",EDGE,"E156"),sQuery(id+"F18.wireOp",EDGE,"E157")])]});
            var Q4;
            Q4=makeQuery(id+"F19.opExtrude","SWEPT_EDGE",EDGE,{"disambiguationData":[OSD([sQuery(id+"F18.wireOp",EDGE,"E148"),sQuery(id+"F18.wireOp",EDGE,"E149")])]});
            fillet(context, id + "F21", {"entities" : qUnion([Q0, Q1, Q2, Q3, Q4]), "radius" : 1 * mm, "tangentPropagation" : true, "allowEdgeOverflow" : false});
        }
    });
